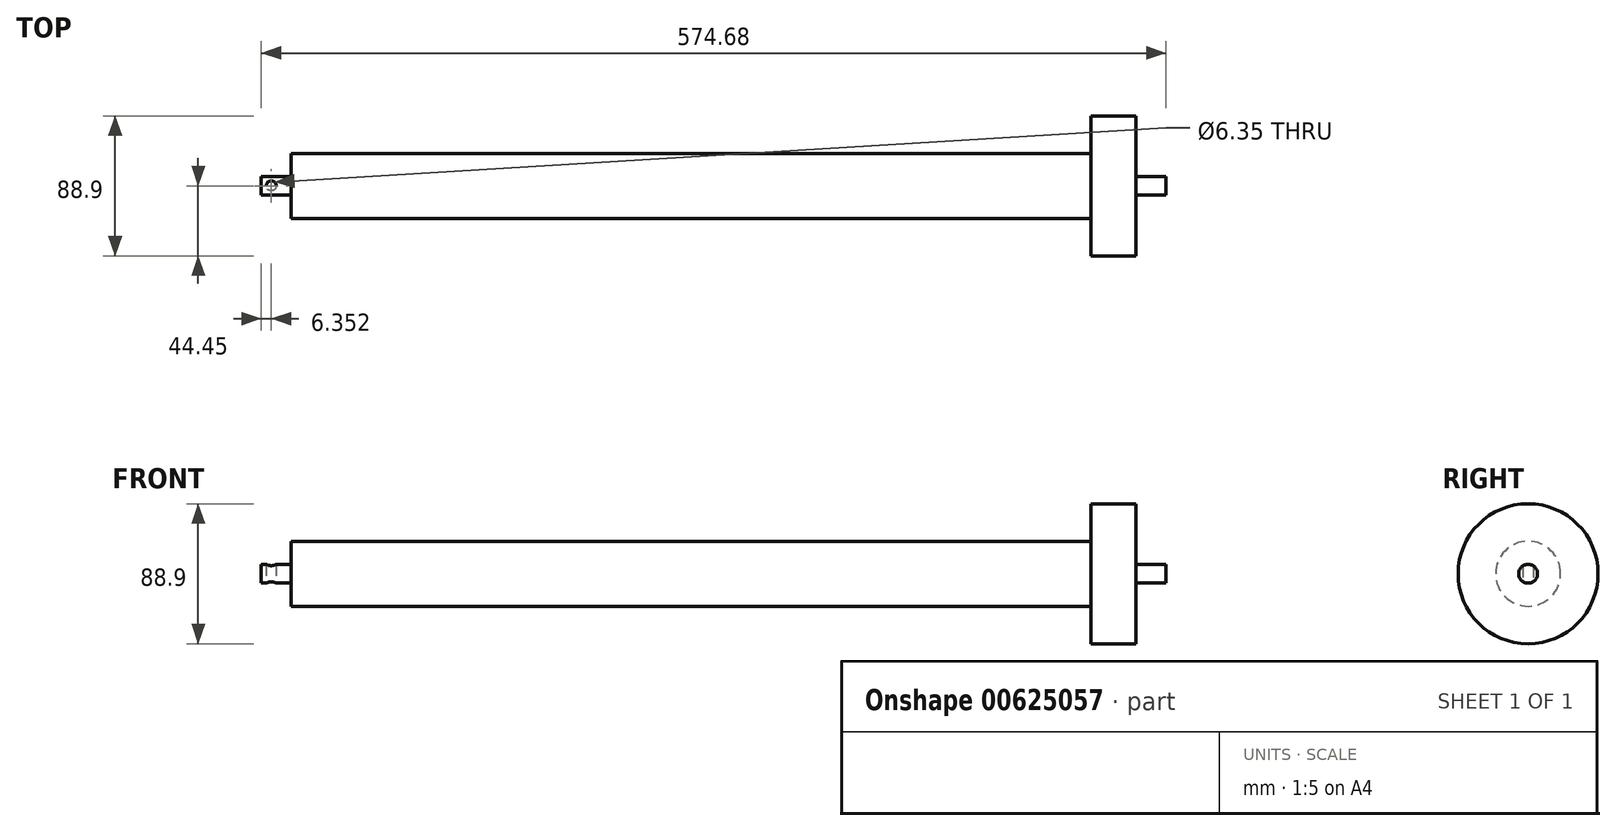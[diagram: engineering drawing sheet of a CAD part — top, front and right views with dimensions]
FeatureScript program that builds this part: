
annotation { "Feature Type Name" : "Feature", "Feature Type Description" : "" }
export const myFeature = defineFeature(function(context is Context, id is Id, definition is map)
    precondition{}
    {
        {
            var Q0;
            Q0=qCreatedBy(makeId("Right.planeOp"),FACE);
            var sketch = newSketch(context, id + "F0", { "sketchPlane" : qUnion([Q0])});
            skCircle(sketch, "E0", {"center": v(0, 0) * mm, "radius": 20.64 * mm});
            skCircle(sketch, "E1", {"center": v(0, 0) * mm, "radius": 6 * mm});
            skCircle(sketch, "E2", {"center": v(0, 0) * mm, "radius": 44.45 * mm});
            skSolve(sketch);
        }
        {
            var Q0;
            Q0=makeQuery(id+"F0.imprint","IMPRINT",FACE,{"disambiguationData":[TD([[makeQuery(id+"F0.imprint","IMPRINT",EDGE,{"derivedFrom":sQuery(id+"F0.wireOp",EDGE,"E0")}),1.0]])]});
            extrude(context, id + "F1", {"entities" : qUnion([Q0]), "endBound" : BoundingType.SYMMETRIC, "depth" : 536.57 * mm, "offsetDistance" : 25.4 * mm});
        }
        {
            var Q0;
            Q0=makeQuery(id+"F0.imprint","IMPRINT",FACE,{"disambiguationData":[TD([[makeQuery(id+"F0.imprint","IMPRINT",EDGE,{"derivedFrom":sQuery(id+"F0.wireOp",EDGE,"E1")}),1.0]])]});
            extrude(context, id + "F2", {"entities" : qUnion([Q0]), "operationType" : NewBodyOperationType.ADD, "endBound" : BoundingType.SYMMETRIC, "depth" : 574.67 * mm, "offsetDistance" : 25.4 * mm});
        }
        {
            var Q0;
            Q0=qCreatedBy(makeId("Top.planeOp"),FACE);
            var sketch = newSketch(context, id + "F3", { "sketchPlane" : qUnion([Q0])});
            skCircle(sketch, "E3", {"center": v(-280.99, 0) * mm, "radius": 3.18 * mm});
            skSolve(sketch);
        }
        {
            var Q0;
            Q0 = qSketchRegion(id + "F3", true);
            var Q1;
            Q1=sQuery(id+"F3.wireOp",EDGE,"E3");
            var Q2;
            Q2=sQuery(id+"F3.wireOp",EDGE,"K1BaaW7G-JvEL-8dHI-NRxC-t8XEmxZXzvFJ");
            extrude(context, id + "F4", {"entities" : qUnion([Q0]), "operationType" : NewBodyOperationType.REMOVE, "surfaceEntities" : qUnion([Q1, Q2]), "endBound" : BoundingType.SYMMETRIC, "depth" : 12.7 * mm, "offsetDistance" : 25.4 * mm});
        }
        {
            var Q0;
            Q0=makeQuery(id+"F0.imprint","IMPRINT",FACE,{"disambiguationData":[TD([[makeQuery(id+"F0.imprint","IMPRINT",EDGE,{"derivedFrom":sQuery(id+"F0.wireOp",EDGE,"E0")}),-1.0]])]});
            var Q1;
            Q1=sQuery(id+"F0.wireOp",EDGE,"E2");
            var Q2;
            Q2=makeQuery(id+"F1.opExtrude","CAP_FACE",FACE,{"disambiguationData":[OSD([sQuery(id+"F0.wireOp",EDGE,"E0"),sQuery(id+"F0.wireOp",EDGE,"E1")])],"isStart":false});
            var Q3;
            Q3=makeQuery(id+"F1.opExtrude","SWEPT_BODY",BODY,{"disambiguationData":[OSD([sQuery(id+"F0.wireOp",EDGE,"E0"),sQuery(id+"F0.wireOp",EDGE,"E1")])]});
            extrude(context, id + "F5", {"entities" : qUnion([Q0]), "operationType" : NewBodyOperationType.ADD, "surfaceEntities" : qUnion([Q1]), "endBound" : BoundingType.UP_TO_SURFACE, "depth" : 28 * mm, "endBoundEntityFace" : qUnion([Q2]), "endBoundEntityBody" : qUnion([Q3]), "offsetDistance" : 25.4 * mm, "hasSecondDirection" : true, "secondDirectionOppositeDirection" : false, "secondDirectionDepth" : 239.71 * mm});
        }
    });
